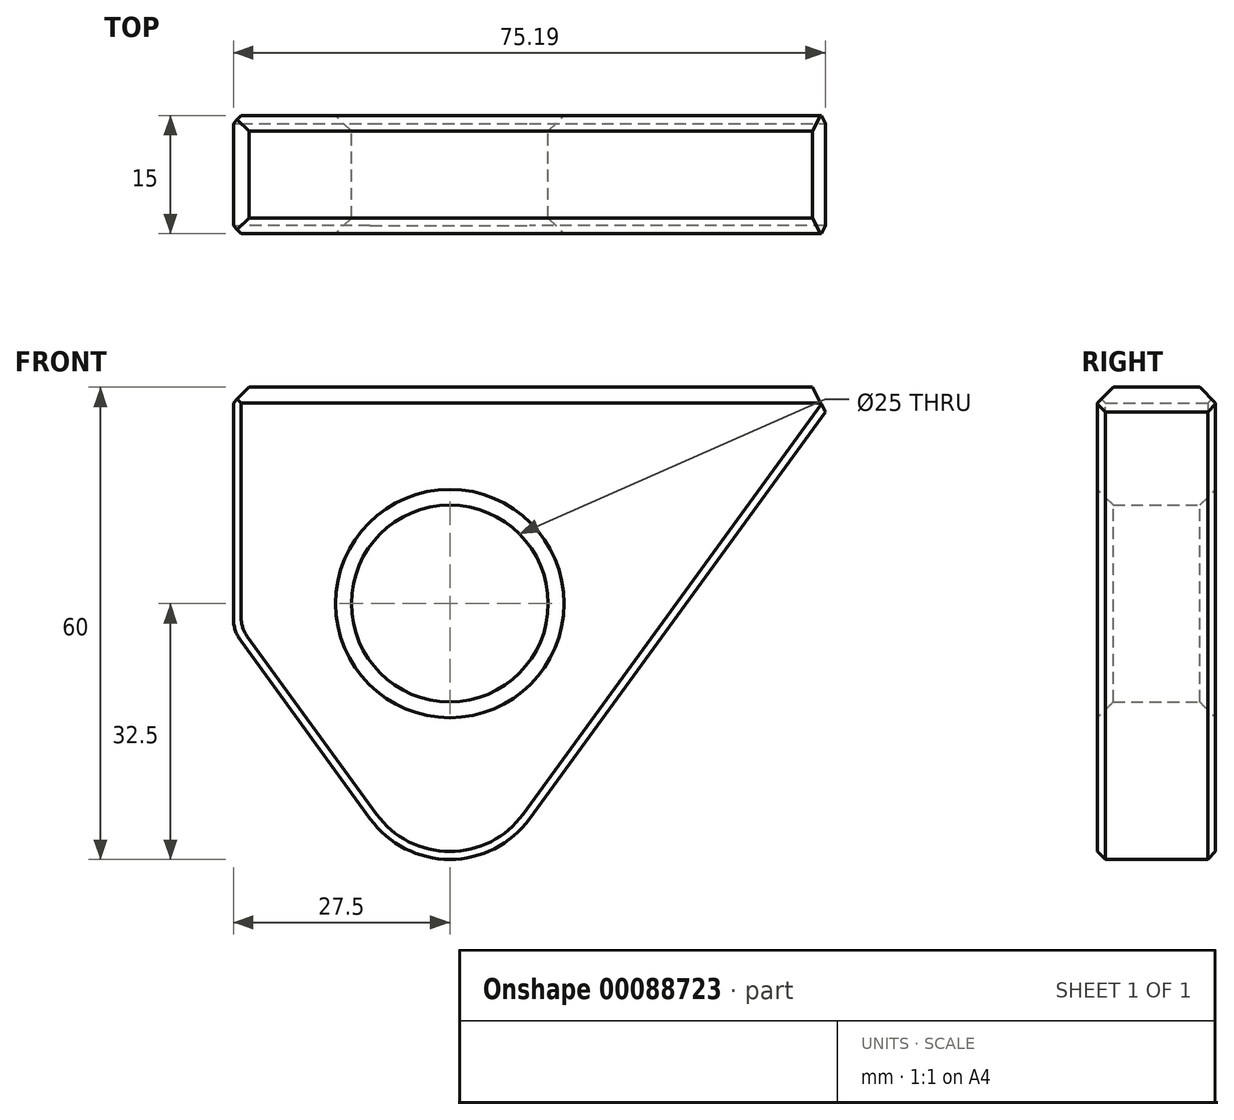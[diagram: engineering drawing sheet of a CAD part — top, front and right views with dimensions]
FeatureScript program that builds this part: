
annotation { "Feature Type Name" : "Feature", "Feature Type Description" : "" }
export const myFeature = defineFeature(function(context is Context, id is Id, definition is map)
    precondition{}
    {
        {
            var Q0;
            Q0=qCreatedBy(makeId("Front.planeOp"),FACE);
            var sketch = newSketch(context, id + "F0", { "sketchPlane" : qUnion([Q0])});
            skLineSegment(sketch, "E0", {"start": v(0, 60) * mm, "end": v(-27.5, 60) * mm});
            skLineSegment(sketch, "E1", {"start": v(0, 60) * mm, "end": v(50, 60) * mm});
            skCircle(sketch, "E2", {"center": v(0, 32.5) * mm, "radius": 12.5 * mm});
            skLineSegment(sketch, "E3", {"start": v(0, 45) * mm, "end": v(0, 60) * mm});
            skArc(sketch, "E4", {"start": v(-10.1, 5.15) * mm, "mid": v(0, 0) * mm, "end": v(10.1, 5.15) * mm});
            skLineSegment(sketch, "E5", {"start": v(50, 60) * mm, "end": v(10.1, 5.15) * mm});
            skLineSegment(sketch, "E6", {"start": v(-27.5, 29.06) * mm, "end": v(-10.1, 5.15) * mm});
            skPoint(sketch, "E7.start.orphan", {"position": v(0, 20) * mm});
            skLineSegment(sketch, "E8", {"start": v(-27.5, 60) * mm, "end": v(-27.5, 29.06) * mm});
            skSolve(sketch);
        }
        {
            var Q0;
            Q0 = qSketchRegion(id + "F0", true);
            var Q1;
            Q1=makeQuery(id+"F0.imprint","IMPRINT",FACE,{"disambiguationData":[TD([[makeQuery(id+"F0.imprint","IMPRINT",EDGE,{"derivedFrom":sQuery(id+"F0.wireOp",EDGE,"E0")}),1.0]])]});
            extrude(context, id + "F1", {"entities" : qUnion([Q0, Q1]), "depth" : 15 * mm});
        }
        {
            var Q0;
            Q0=makeQuery(id+"F1.opExtrude","SWEPT_FACE",FACE,{"disambiguationData":[OSD([sQuery(id+"F0.wireOp",EDGE,"E0"),sQuery(id+"F0.wireOp",EDGE,"E1")])]});
            var Q1;
            Q1=makeQuery(id+"F1.opExtrude","SWEPT_FACE",FACE,{"disambiguationData":[OSD([sQuery(id+"F0.wireOp",EDGE,"E2")])]});
            chamfer(context, id + "F2", {"entities" : qUnion([Q0, Q1]), "width" : 2 * mm, "tangentPropagation" : true});
        }
        {
            var Q0;
            Q0=makeQuery(id+"F1.opExtrude","SWEPT_EDGE",EDGE,{"disambiguationData":[OSD([sQuery(id+"F0.wireOp",EDGE,"E6"),sQuery(id+"F0.wireOp",EDGE,"E8")])]});
            fillet(context, id + "F3", {"entities" : qUnion([Q0]), "radius" : 5 * mm, "tangentPropagation" : true, "allowEdgeOverflow" : false});
        }
        {
            var Q0;
            Q0=makeQuery(id+"F1.opExtrude","CAP_EDGE",EDGE,{"disambiguationData":[OSD([sQuery(id+"F0.wireOp",EDGE,"E5")])],"isStart":false});
            var Q1;
            Q1=makeQuery(id+"F1.opExtrude","CAP_EDGE",EDGE,{"disambiguationData":[OSD([sQuery(id+"F0.wireOp",EDGE,"E5")])],"isStart":true});
            chamfer(context, id + "F4", {"entities" : qUnion([Q0, Q1]), "width" : 1 * mm, "tangentPropagation" : true});
        }
    });
